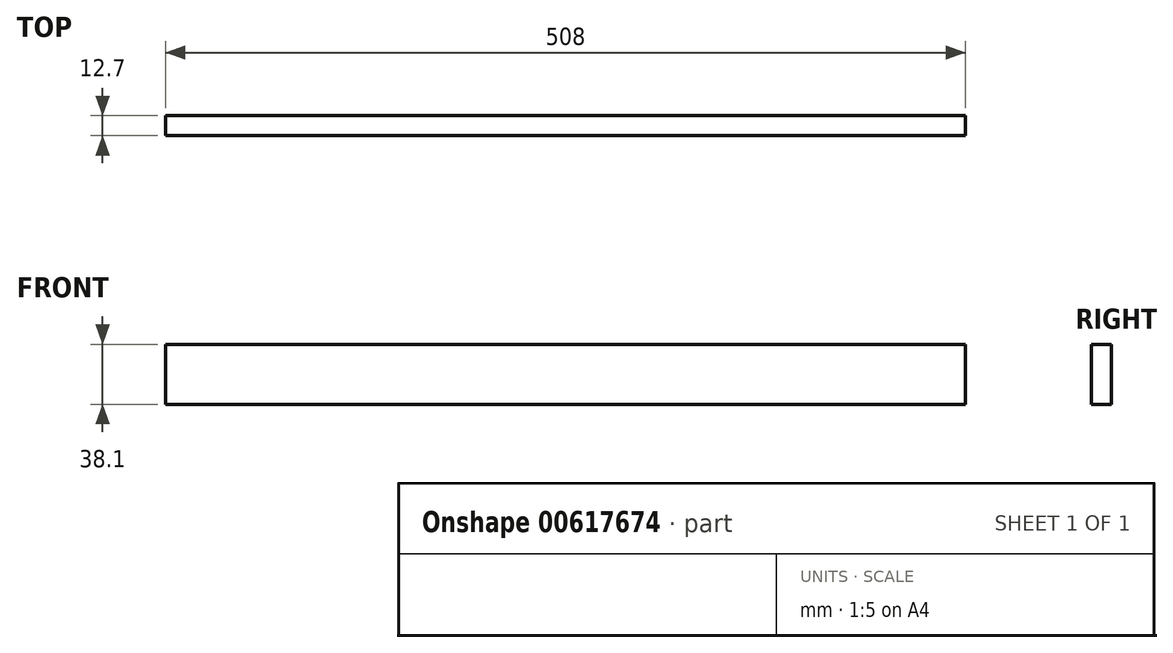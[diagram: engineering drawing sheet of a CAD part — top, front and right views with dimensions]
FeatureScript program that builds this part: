
annotation { "Feature Type Name" : "Feature", "Feature Type Description" : "" }
export const myFeature = defineFeature(function(context is Context, id is Id, definition is map)
    precondition{}
    {
        {
            var Q0;
            Q0=qCreatedBy(makeId("Front.planeOp"),FACE);
            var sketch = newSketch(context, id + "F0", { "sketchPlane" : qUnion([Q0])});
            skLineSegment(sketch, "E0.bottom", {"start": v(441.27, 2.9) * mm, "end": v(-66.73, 2.9) * mm});
            skLineSegment(sketch, "E0.top", {"start": v(441.27, 41) * mm, "end": v(-66.73, 41) * mm});
            skLineSegment(sketch, "E0.left", {"start": v(441.27, 2.9) * mm, "end": v(441.27, 41) * mm});
            skLineSegment(sketch, "E0.right", {"start": v(-66.73, 2.9) * mm, "end": v(-66.73, 41) * mm});
            skPoint(sketch, "E0.middle", {"position": v(187.27, 21.95) * mm});
            skSolve(sketch);
        }
        {
            var Q0;
            Q0 = qSketchRegion(id + "F0", true);
            extrude(context, id + "F1", {"entities" : qUnion([Q0]), "endBound" : BoundingType.SYMMETRIC, "depth" : 12.7 * mm, "offsetDistance" : 25.4 * mm});
        }
    });
